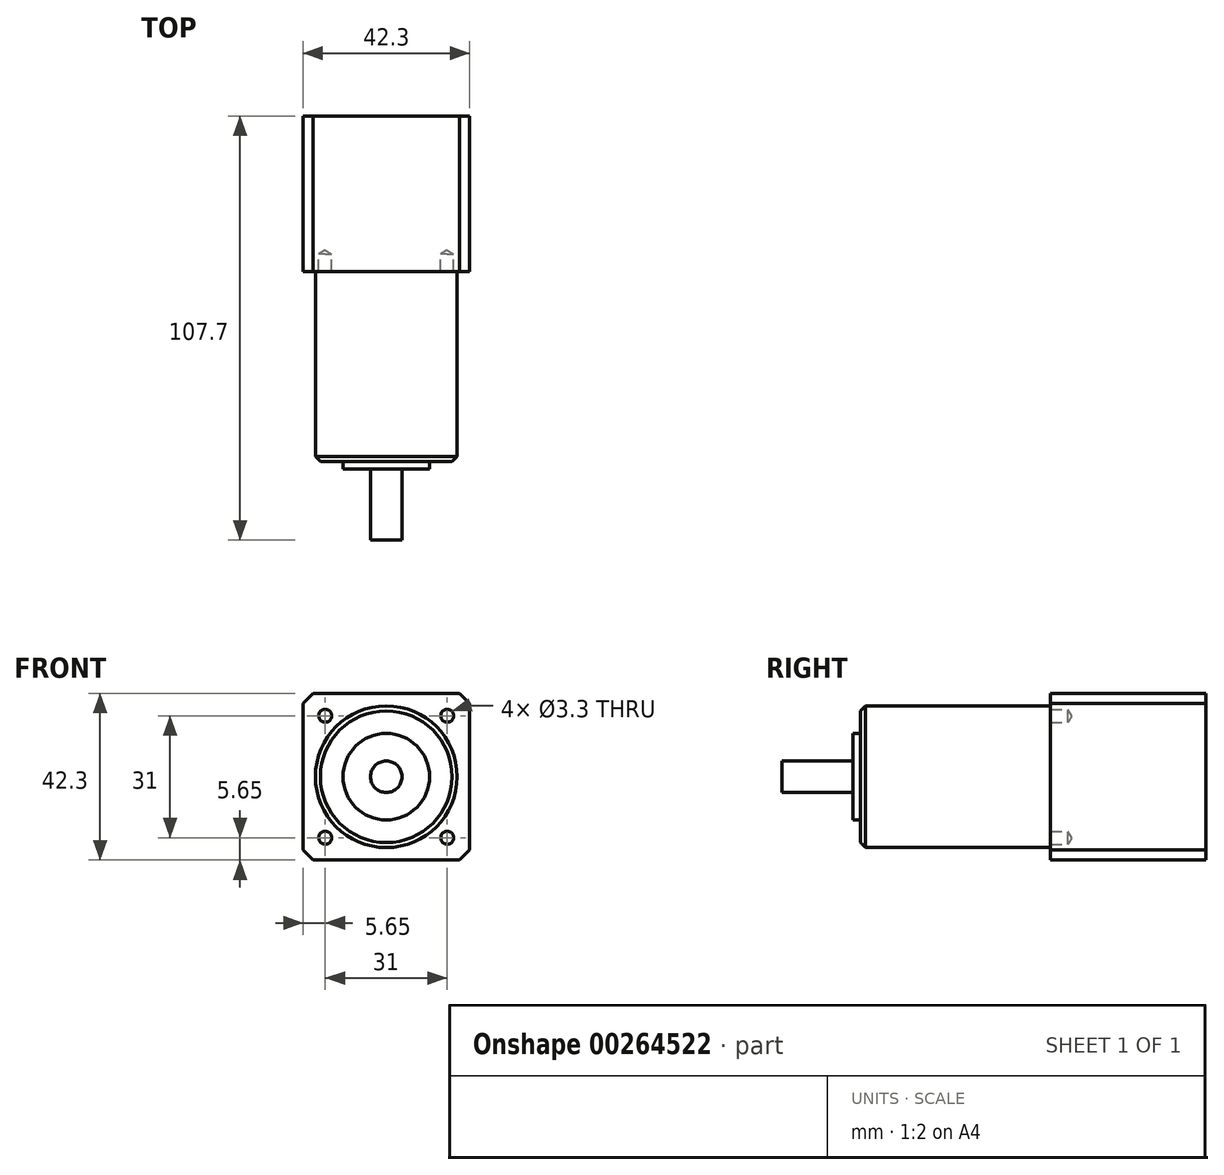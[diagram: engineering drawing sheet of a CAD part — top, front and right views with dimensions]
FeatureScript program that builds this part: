
annotation { "Feature Type Name" : "Feature", "Feature Type Description" : "" }
export const myFeature = defineFeature(function(context is Context, id is Id, definition is map)
    precondition{}
    {
        {
            var Q0;
            Q0=qCreatedBy(makeId("Front.planeOp"),FACE);
            var sketch = newSketch(context, id + "F0", { "sketchPlane" : qUnion([Q0])});
            skLineSegment(sketch, "E0.bottom", {"start": v(-21.15, 21.15) * mm, "end": v(21.15, 21.15) * mm});
            skLineSegment(sketch, "E0.top", {"start": v(-21.15, -21.15) * mm, "end": v(21.15, -21.15) * mm});
            skLineSegment(sketch, "E0.left", {"start": v(-21.15, 21.15) * mm, "end": v(-21.15, -21.15) * mm});
            skLineSegment(sketch, "E0.right", {"start": v(21.15, 21.15) * mm, "end": v(21.15, -21.15) * mm});
            skPoint(sketch, "E0.middle", {"position": v(0, 0) * mm});
            skSolve(sketch);
        }
        {
            var Q0;
            Q0 = qSketchRegion(id + "F0", true);
            extrude(context, id + "F1", {"entities" : qUnion([Q0]), "depth" : 39.5 * mm, "offsetDistance" : 25.4 * mm, "symmetric" : true});
        }
        {
            var Q0;
            Q0=makeQuery(id+"F1.opExtrude","SWEPT_EDGE",EDGE,{"disambiguationData":[OSD([sQuery(id+"F0.wireOp",EDGE,"E0.bottom"),sQuery(id+"F0.wireOp",EDGE,"E0.right")])]});
            var Q1;
            Q1=makeQuery(id+"F1.opExtrude","SWEPT_EDGE",EDGE,{"disambiguationData":[OSD([sQuery(id+"F0.wireOp",EDGE,"E0.bottom"),sQuery(id+"F0.wireOp",EDGE,"E0.left")])]});
            var Q2;
            Q2=makeQuery(id+"F1.opExtrude","SWEPT_EDGE",EDGE,{"disambiguationData":[OSD([sQuery(id+"F0.wireOp",EDGE,"E0.top"),sQuery(id+"F0.wireOp",EDGE,"E0.left")])]});
            var Q3;
            Q3=makeQuery(id+"F1.opExtrude","SWEPT_EDGE",EDGE,{"disambiguationData":[OSD([sQuery(id+"F0.wireOp",EDGE,"E0.top"),sQuery(id+"F0.wireOp",EDGE,"E0.right")])]});
            chamfer(context, id + "F2", {"entities" : qUnion([Q0, Q1, Q2, Q3]), "width" : 2.54 * mm, "tangentPropagation" : true});
        }
        {
            var Q0;
            Q0=makeQuery(id+"F1.opExtrude","CAP_FACE",FACE,{"disambiguationData":[OSD([sQuery(id+"F0.wireOp",EDGE,"E0.bottom"),sQuery(id+"F0.wireOp",EDGE,"E0.top"),sQuery(id+"F0.wireOp",EDGE,"E0.left"),sQuery(id+"F0.wireOp",EDGE,"E0.right")])],"isStart":false});
            var sketch = newSketch(context, id + "F3", { "sketchPlane" : qUnion([Q0])});
            skLineSegment(sketch, "E1.bottom", {"start": v(-15.5, 15.5) * mm, "end": v(15.5, 15.5) * mm});
            skLineSegment(sketch, "E1.top", {"start": v(-15.5, -15.5) * mm, "end": v(15.5, -15.5) * mm});
            skLineSegment(sketch, "E1.left", {"start": v(-15.5, 15.5) * mm, "end": v(-15.5, -15.5) * mm});
            skLineSegment(sketch, "E1.right", {"start": v(15.5, 15.5) * mm, "end": v(15.5, -15.5) * mm});
            skPoint(sketch, "E1.middle", {"position": v(0, 0) * mm});
            skPoint(sketch, "E2", {"position": v(15.5, 15.5) * mm});
            skPoint(sketch, "E3", {"position": v(-15.5, 15.5) * mm});
            skPoint(sketch, "E4", {"position": v(-15.5, -15.5) * mm});
            skPoint(sketch, "E5", {"position": v(15.5, -15.5) * mm});
            skSolve(sketch);
        }
        {
            var Q0;
            Q0=sQuery(id+"F3.wireOp",VERTEX,"E2");
            var Q1;
            Q1=sQuery(id+"F3.wireOp",VERTEX,"E5");
            var Q2;
            Q2=sQuery(id+"F3.wireOp",VERTEX,"E4");
            var Q3;
            Q3=sQuery(id+"F3.wireOp",VERTEX,"E3");
            var Q4;
            Q4=makeQuery(id+"F1.opExtrude","SWEPT_BODY",BODY,{"disambiguationData":[OSD([sQuery(id+"F0.wireOp",EDGE,"E0.bottom"),sQuery(id+"F0.wireOp",EDGE,"E0.top"),sQuery(id+"F0.wireOp",EDGE,"E0.left"),sQuery(id+"F0.wireOp",EDGE,"E0.right")])]});
            hole(context, id + "F4", {"style" : HoleStyle.SIMPLE, "endStyle" : HoleEndStyle.BLIND, "standardTappedOrClearance" : lookupTablePath({ "standard" : "ISO", "fit" : "Normal", "size" : "M3", "type" : "Clearance" }), "standardBlindInLast" : lookupTablePath({ "fit" : "Standard", "standard" : "ISO", "size" : "M3", "type" : "Clearance" }), "holeDiameter" : 3.3 * mm, "majorDiameter" : 6.35 * mm, "holeDepth" : 4.5 * mm, "isTappedThrough" : true, "tappedDepth" : 12.7 * mm, "tapClearance" : 3, "locations" : qUnion([Q0, Q1, Q2, Q3]), "scope" : qUnion([Q4]), "startStyle" : HoleStartStyle.PART});
        }
        {
            var Q0;
            Q0=makeQuery(id+"F1.opExtrude","CAP_FACE",FACE,{"disambiguationData":[OSD([sQuery(id+"F0.wireOp",EDGE,"E0.bottom"),sQuery(id+"F0.wireOp",EDGE,"E0.top"),sQuery(id+"F0.wireOp",EDGE,"E0.left"),sQuery(id+"F0.wireOp",EDGE,"E0.right")])],"isStart":false});
            var sketch = newSketch(context, id + "F5", { "sketchPlane" : qUnion([Q0])});
            skCircle(sketch, "E6", {"center": v(0, 0) * mm, "radius": 18 * mm});
            skSolve(sketch);
        }
        {
            var Q0;
            Q0 = qSketchRegion(id + "F5", true);
            extrude(context, id + "F6", {"entities" : qUnion([Q0]), "operationType" : NewBodyOperationType.ADD, "depth" : 48.2 * mm, "offsetDistance" : 25.4 * mm});
        }
        {
            var Q0;
            Q0=makeQuery(id+"F6.opExtrude","CAP_FACE",FACE,{"disambiguationData":[OSD([sQuery(id+"F5.wireOp",EDGE,"E6")])],"isStart":false});
            var sketch = newSketch(context, id + "F7", { "sketchPlane" : qUnion([Q0])});
            skCircle(sketch, "E7", {"center": v(0, 0) * mm, "radius": 11 * mm});
            skSolve(sketch);
        }
        {
            var Q0;
            Q0 = qSketchRegion(id + "F7", true);
            extrude(context, id + "F8", {"entities" : qUnion([Q0]), "operationType" : NewBodyOperationType.ADD, "depth" : 2 * mm, "offsetDistance" : 25.4 * mm});
        }
        {
            var Q0;
            Q0=makeQuery(id+"F8.opExtrude","CAP_FACE",FACE,{"disambiguationData":[OSD([sQuery(id+"F7.wireOp",EDGE,"E7")])],"isStart":false});
            var sketch = newSketch(context, id + "F9", { "sketchPlane" : qUnion([Q0])});
            skCircle(sketch, "E8", {"center": v(0, 0) * mm, "radius": 4 * mm});
            skSolve(sketch);
        }
        {
            var Q0;
            Q0 = qSketchRegion(id + "F9", true);
            extrude(context, id + "F10", {"entities" : qUnion([Q0]), "operationType" : NewBodyOperationType.ADD, "depth" : 18 * mm, "offsetDistance" : 25.4 * mm});
        }
        {
            var Q0;
            Q0=makeQuery(id+"F6.opExtrude","CAP_EDGE",EDGE,{"disambiguationData":[OSD([sQuery(id+"F5.wireOp",EDGE,"E6")])],"isStart":false});
            chamfer(context, id + "F11", {"entities" : qUnion([Q0]), "width" : 1.27 * mm, "tangentPropagation" : true});
        }
    });
